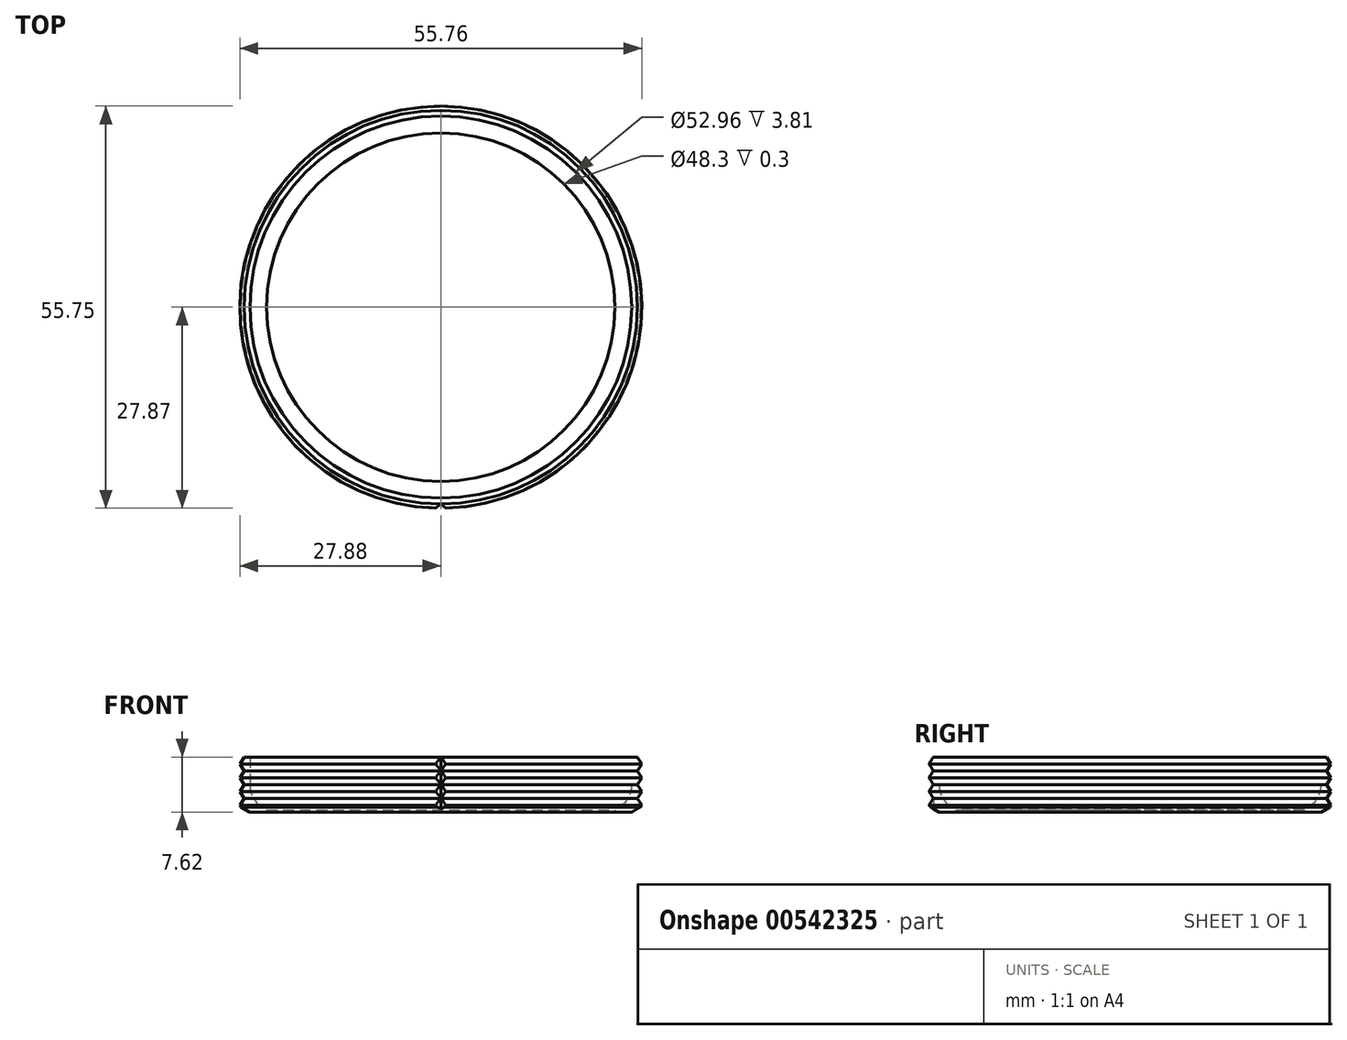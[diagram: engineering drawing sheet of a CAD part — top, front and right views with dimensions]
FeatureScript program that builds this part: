
annotation { "Feature Type Name" : "Feature", "Feature Type Description" : "" }
export const myFeature = defineFeature(function(context is Context, id is Id, definition is map)
    precondition{}
    {
        {
            var Q0;
            Q0=qCreatedBy(makeId("Front.planeOp"),FACE);
            var sketch = newSketch(context, id + "F0", { "sketchPlane" : qUnion([Q0])});
            skLineSegment(sketch, "E0", {"start": v(0, 0) * mm, "end": v(0, 3.64) * mm, "construction": true});
            skLineSegment(sketch, "E1", {"start": v(27.28, 0) * mm, "end": v(27.28, 7.62) * mm});
            skLineSegment(sketch, "E2", {"start": v(27.28, 7.62) * mm, "end": v(26.48, 7.62) * mm});
            skLineSegment(sketch, "E3", {"start": v(26.48, 7.62) * mm, "end": v(26.48, 3.81) * mm});
            skArc(sketch, "E4", {"start": v(24.15, 0.3) * mm, "mid": v(25.84, 1.7) * mm, "end": v(26.48, 3.81) * mm});
            skLineSegment(sketch, "E5", {"start": v(24.15, 0) * mm, "end": v(27.28, 0) * mm});
            skLineSegment(sketch, "E6", {"start": v(24.15, 0) * mm, "end": v(24.15, 0.3) * mm});
            skPoint(sketch, "E7.orphan", {"position": v(22.67, 0) * mm});
            skLineSegment(sketch, "E8", {"start": v(27.88, 0) * mm, "end": v(27.88, 7.62) * mm, "construction": true});
            skLineSegment(sketch, "E9", {"start": v(27.28, 0) * mm, "end": v(27.88, 0.95) * mm});
            skLineSegment(sketch, "E10", {"start": v(27.88, 0.95) * mm, "end": v(27.28, 1.9) * mm});
            skLineSegment(sketch, "E11", {"start": v(27.28, 1.9) * mm, "end": v(27.88, 2.86) * mm});
            skLineSegment(sketch, "E12", {"start": v(27.88, 2.86) * mm, "end": v(27.28, 3.81) * mm});
            skLineSegment(sketch, "E13", {"start": v(27.28, 3.81) * mm, "end": v(27.88, 4.76) * mm});
            skLineSegment(sketch, "E14", {"start": v(27.88, 4.76) * mm, "end": v(27.28, 5.72) * mm});
            skLineSegment(sketch, "E15", {"start": v(27.28, 5.72) * mm, "end": v(27.88, 6.67) * mm});
            skLineSegment(sketch, "E16", {"start": v(27.88, 6.67) * mm, "end": v(27.28, 7.62) * mm});
            skSolve(sketch);
        }
        {
            var Q0;
            Q0 = qSketchRegion(id + "F0", true);
            var Q1;
            Q1=sQuery(id+"F0.wireOp",EDGE,"E0");
            revolve(context, id + "F1", {"entities" : qUnion([Q0]), "axis" : qUnion([Q1]), "revolveType" : RevolveType.FULL});
        }
        {
            var Q0;
            Q0=qCreatedBy(makeId("Top.planeOp"),FACE);
            var sketch = newSketch(context, id + "F2", { "sketchPlane" : qUnion([Q0])});
            skPoint(sketch, "E17", {"position": v(0, -27.28) * mm});
            skPoint(sketch, "E18", {"position": v(0, -27.88) * mm});
            skLineSegment(sketch, "E19", {"start": v(0, -27.28) * mm, "end": v(-0.73, -27.88) * mm});
            skLineSegment(sketch, "E20", {"start": v(-0.73, -27.88) * mm, "end": v(0.73, -27.88) * mm});
            skLineSegment(sketch, "E21", {"start": v(0.73, -27.88) * mm, "end": v(0, -27.28) * mm});
            skLineSegment(sketch, "E22", {"start": v(-0.73, -27.88) * mm, "end": v(0, 0) * mm, "construction": true});
            skLineSegment(sketch, "E23", {"start": v(0, 0) * mm, "end": v(0.73, -27.88) * mm, "construction": true});
            skSolve(sketch);
        }
        {
            var Q0;
            Q0 = qSketchRegion(id + "F2", true);
            extrude(context, id + "F3", {"entities" : qUnion([Q0]), "operationType" : NewBodyOperationType.REMOVE, "endBound" : BoundingType.THROUGH_ALL, "depth" : 25.4 * mm, "offsetDistance" : 25.4 * mm});
        }
        {
            var Q0;
            Q0=qCreatedBy(makeId("Front.planeOp"),FACE);
            var sketch = newSketch(context, id + "F4", { "sketchPlane" : qUnion([Q0])});
            skLineSegment(sketch, "E24", {"start": v(26.5, 0) * mm, "end": v(27.72, 0.7) * mm});
            skLineSegment(sketch, "E25", {"start": v(27.72, 0.7) * mm, "end": v(27.72, 0) * mm});
            skLineSegment(sketch, "E26", {"start": v(27.72, 0) * mm, "end": v(26.5, 0) * mm});
            skPoint(sketch, "E27", {"position": v(27.72, 0.7) * mm});
            skSolve(sketch);
        }
        {
            var Q0;
            Q0 = qSketchRegion(id + "F4", true);
            var Q1;
            Q1=sQuery(id+"F0.wireOp",EDGE,"E0");
            revolve(context, id + "F5", {"operationType" : NewBodyOperationType.REMOVE, "entities" : qUnion([Q0]), "axis" : qUnion([Q1]), "revolveType" : RevolveType.FULL, "oppositeDirection" : true});
        }
    });
